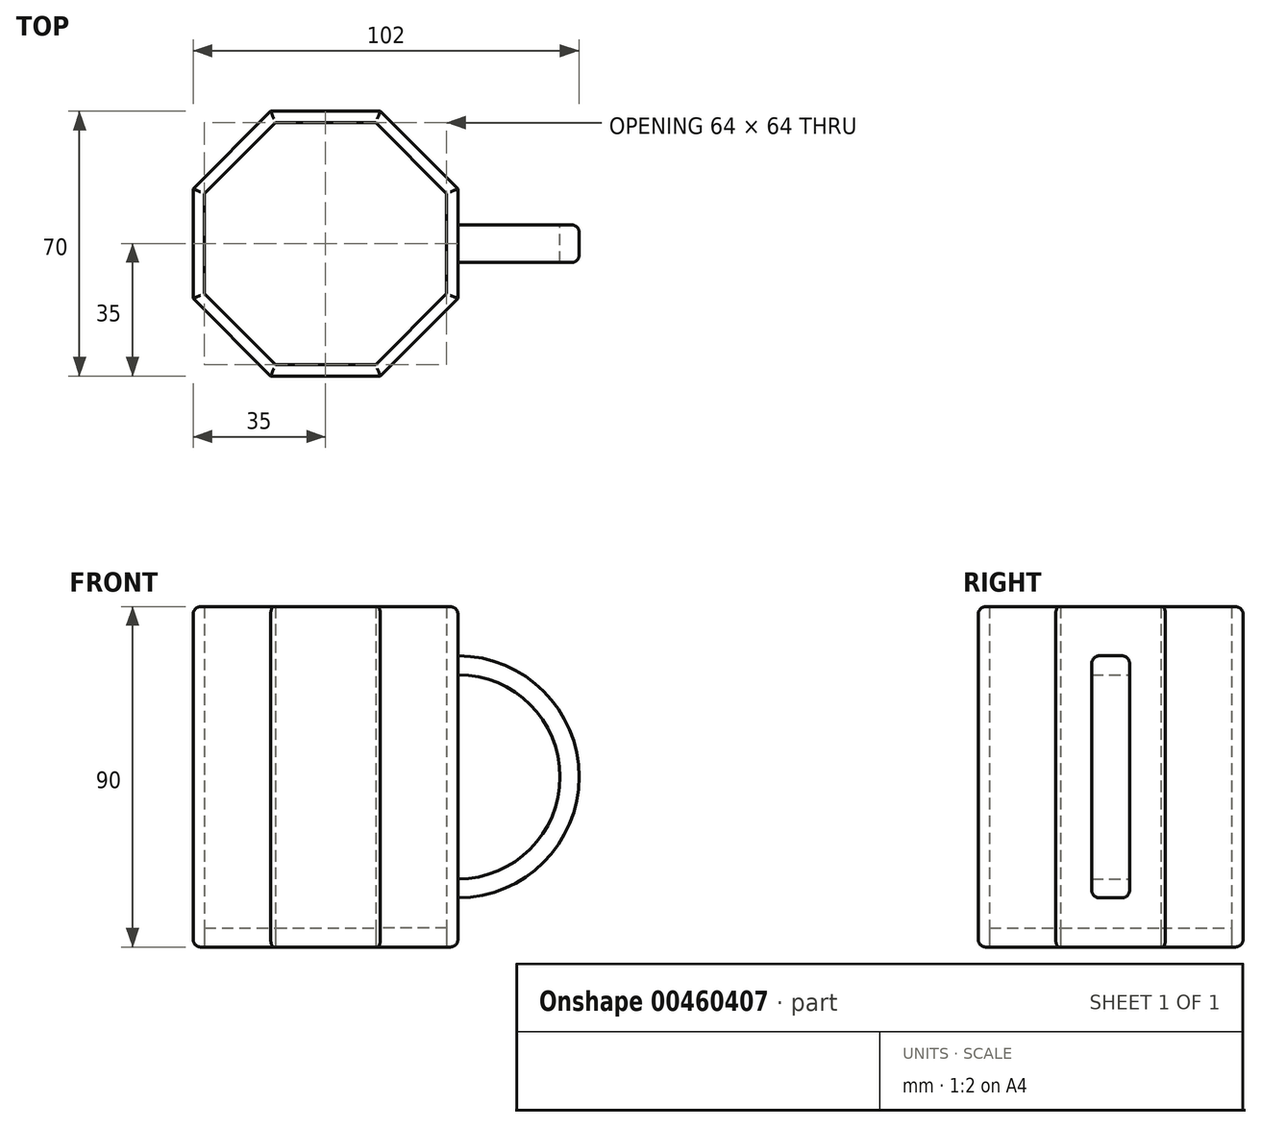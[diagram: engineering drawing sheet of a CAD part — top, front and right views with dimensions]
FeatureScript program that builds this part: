
annotation { "Feature Type Name" : "Feature", "Feature Type Description" : "" }
export const myFeature = defineFeature(function(context is Context, id is Id, definition is map)
    precondition{}
    {
        {
            var Q0;
            Q0=qCreatedBy(makeId("Top.planeOp"),FACE);
            var sketch = newSketch(context, id + "F0", { "sketchPlane" : qUnion([Q0])});
            skCircle(sketch, "E0.cCircle", {"center": v(0, 0) * mm, "radius": 35 * mm, "construction": true});
            skLineSegment(sketch, "E0.0", {"start": v(-14.5, 35) * mm, "end": v(14.5, 35) * mm});
            skLineSegment(sketch, "E0.1", {"start": v(14.5, 35) * mm, "end": v(35, 14.5) * mm});
            skLineSegment(sketch, "E0.2", {"start": v(35, 14.5) * mm, "end": v(35, -14.5) * mm});
            skLineSegment(sketch, "E0.3", {"start": v(35, -14.5) * mm, "end": v(14.5, -35) * mm});
            skLineSegment(sketch, "E0.4", {"start": v(14.5, -35) * mm, "end": v(-14.5, -35) * mm});
            skLineSegment(sketch, "E0.5", {"start": v(-14.5, -35) * mm, "end": v(-35, -14.5) * mm});
            skLineSegment(sketch, "E0.6", {"start": v(-35, -14.5) * mm, "end": v(-35, 14.5) * mm});
            skLineSegment(sketch, "E0.7", {"start": v(-35, 14.5) * mm, "end": v(-14.5, 35) * mm});
            skPoint(sketch, "E0.0.midPoint", {"position": v(0, 35) * mm});
            skCircle(sketch, "E1.cCircle", {"center": v(0, 0) * mm, "radius": 32 * mm, "construction": true});
            skLineSegment(sketch, "E1.0", {"start": v(-13.25, 32) * mm, "end": v(13.25, 32) * mm});
            skLineSegment(sketch, "E1.1", {"start": v(13.25, 32) * mm, "end": v(32, 13.25) * mm});
            skLineSegment(sketch, "E1.2", {"start": v(32, 13.25) * mm, "end": v(32, -13.25) * mm});
            skLineSegment(sketch, "E1.3", {"start": v(32, -13.25) * mm, "end": v(13.25, -32) * mm});
            skLineSegment(sketch, "E1.4", {"start": v(13.25, -32) * mm, "end": v(-13.25, -32) * mm});
            skLineSegment(sketch, "E1.5", {"start": v(-13.25, -32) * mm, "end": v(-32, -13.25) * mm});
            skLineSegment(sketch, "E1.6", {"start": v(-32, -13.25) * mm, "end": v(-32, 13.25) * mm});
            skLineSegment(sketch, "E1.7", {"start": v(-32, 13.25) * mm, "end": v(-13.25, 32) * mm});
            skPoint(sketch, "E1.0.midPoint", {"position": v(0, 32) * mm});
            skSolve(sketch);
        }
        {
            var Q0;
            Q0 = qSketchRegion(id + "F0", true);
            extrude(context, id + "F1", {"entities" : qUnion([Q0]), "depth" : 90 * mm});
        }
        {
            var Q0;
            Q0=makeQuery(id+"F0.imprint","IMPRINT",FACE,{"disambiguationData":[TD([[makeQuery(id+"F0.imprint","IMPRINT",EDGE,{"derivedFrom":sQuery(id+"F0.wireOp",EDGE,"E1.0")}),-1.0]])]});
            extrude(context, id + "F2", {"entities" : qUnion([Q0]), "depth" : 5 * mm});
        }
        {
            var Q0;
            Q0=qCreatedBy(makeId("Front.planeOp"),FACE);
            var sketch = newSketch(context, id + "F3", { "sketchPlane" : qUnion([Q0])});
            skPoint(sketch, "E2", {"position": v(35, 45) * mm});
            skArc(sketch, "E3", {"start": v(35, 77) * mm, "mid": v(67, 45) * mm, "end": v(35, 13) * mm});
            skLineSegment(sketch, "E4", {"start": v(35, 18) * mm, "end": v(35, 13) * mm});
            skArc(sketch, "E5", {"start": v(35, 18) * mm, "mid": v(62, 45) * mm, "end": v(35, 72) * mm});
            skLineSegment(sketch, "E6", {"start": v(35, 77) * mm, "end": v(35, 72) * mm});
            skSolve(sketch);
        }
        {
            var Q0;
            Q0 = qSketchRegion(id + "F3", true);
            extrude(context, id + "F4", {"entities" : qUnion([Q0]), "depth" : 5 * mm, "hasSecondDirection" : true, "secondDirectionOppositeDirection" : true, "secondDirectionDepth" : 5 * mm, "offsetDistance" : 25 * mm});
        }
        {
            var Q0;
            Q0=makeQuery(id+"F1.opExtrude","CAP_EDGE",EDGE,{"disambiguationData":[OSD([sQuery(id+"F0.wireOp",EDGE,"E0.1")])],"isStart":false});
            var Q1;
            Q1=makeQuery(id+"F1.opExtrude","CAP_EDGE",EDGE,{"disambiguationData":[OSD([sQuery(id+"F0.wireOp",EDGE,"E0.0")])],"isStart":false});
            var Q2;
            Q2=makeQuery(id+"F1.opExtrude","CAP_EDGE",EDGE,{"disambiguationData":[OSD([sQuery(id+"F0.wireOp",EDGE,"E0.7")])],"isStart":false});
            var Q3;
            Q3=makeQuery(id+"F1.opExtrude","CAP_EDGE",EDGE,{"disambiguationData":[OSD([sQuery(id+"F0.wireOp",EDGE,"E0.6")])],"isStart":false});
            var Q4;
            Q4=makeQuery(id+"F1.opExtrude","CAP_EDGE",EDGE,{"disambiguationData":[OSD([sQuery(id+"F0.wireOp",EDGE,"E0.5")])],"isStart":false});
            var Q5;
            Q5=makeQuery(id+"F1.opExtrude","CAP_EDGE",EDGE,{"disambiguationData":[OSD([sQuery(id+"F0.wireOp",EDGE,"E0.4")])],"isStart":false});
            var Q6;
            Q6=makeQuery(id+"F1.opExtrude","CAP_EDGE",EDGE,{"disambiguationData":[OSD([sQuery(id+"F0.wireOp",EDGE,"E0.3")])],"isStart":false});
            var Q7;
            Q7=makeQuery(id+"F1.opExtrude","CAP_EDGE",EDGE,{"disambiguationData":[OSD([sQuery(id+"F0.wireOp",EDGE,"E0.2")])],"isStart":false});
            var Q8;
            Q8=makeQuery(id+"F4.opExtrude","CAP_EDGE",EDGE,{"disambiguationData":[OSD([sQuery(id+"F3.wireOp",EDGE,"E3")])],"isStart":false});
            var Q9;
            Q9=makeQuery(id+"F4.opExtrude","CAP_EDGE",EDGE,{"disambiguationData":[OSD([sQuery(id+"F3.wireOp",EDGE,"E3")])],"isStart":true});
            var Q10;
            Q10=makeQuery(id+"F4.opExtrude","CAP_EDGE",EDGE,{"disambiguationData":[OSD([sQuery(id+"F3.wireOp",EDGE,"slvdy9hj-Dx2M-fsP7-mLh9-FjnBijz6HTeI")])],"isStart":false});
            var Q11;
            Q11=makeQuery(id+"F1.opExtrude","CAP_EDGE",EDGE,{"disambiguationData":[OSD([sQuery(id+"F0.wireOp",EDGE,"E0.2")])],"isStart":true});
            var Q12;
            Q12=makeQuery(id+"F1.opExtrude","CAP_EDGE",EDGE,{"disambiguationData":[OSD([sQuery(id+"F0.wireOp",EDGE,"E0.1")])],"isStart":true});
            var Q13;
            Q13=makeQuery(id+"F1.opExtrude","CAP_EDGE",EDGE,{"disambiguationData":[OSD([sQuery(id+"F0.wireOp",EDGE,"E0.0")])],"isStart":true});
            var Q14;
            Q14=makeQuery(id+"F1.opExtrude","CAP_EDGE",EDGE,{"disambiguationData":[OSD([sQuery(id+"F0.wireOp",EDGE,"E0.7")])],"isStart":true});
            var Q15;
            Q15=makeQuery(id+"F1.opExtrude","CAP_EDGE",EDGE,{"disambiguationData":[OSD([sQuery(id+"F0.wireOp",EDGE,"E0.6")])],"isStart":true});
            var Q16;
            Q16=makeQuery(id+"F1.opExtrude","CAP_EDGE",EDGE,{"disambiguationData":[OSD([sQuery(id+"F0.wireOp",EDGE,"E0.5")])],"isStart":true});
            var Q17;
            Q17=makeQuery(id+"F1.opExtrude","CAP_EDGE",EDGE,{"disambiguationData":[OSD([sQuery(id+"F0.wireOp",EDGE,"E0.4")])],"isStart":true});
            var Q18;
            Q18=makeQuery(id+"F1.opExtrude","CAP_EDGE",EDGE,{"disambiguationData":[OSD([sQuery(id+"F0.wireOp",EDGE,"E0.3")])],"isStart":true});
            fillet(context, id + "F5", {"entities" : qUnion([Q0, Q1, Q2, Q3, Q4, Q5, Q6, Q7, Q8, Q9, Q10, Q11, Q12, Q13, Q14, Q15, Q16, Q17, Q18]), "radius" : 2 * mm, "tangentPropagation" : true, "allowEdgeOverflow" : false});
        }
    });
